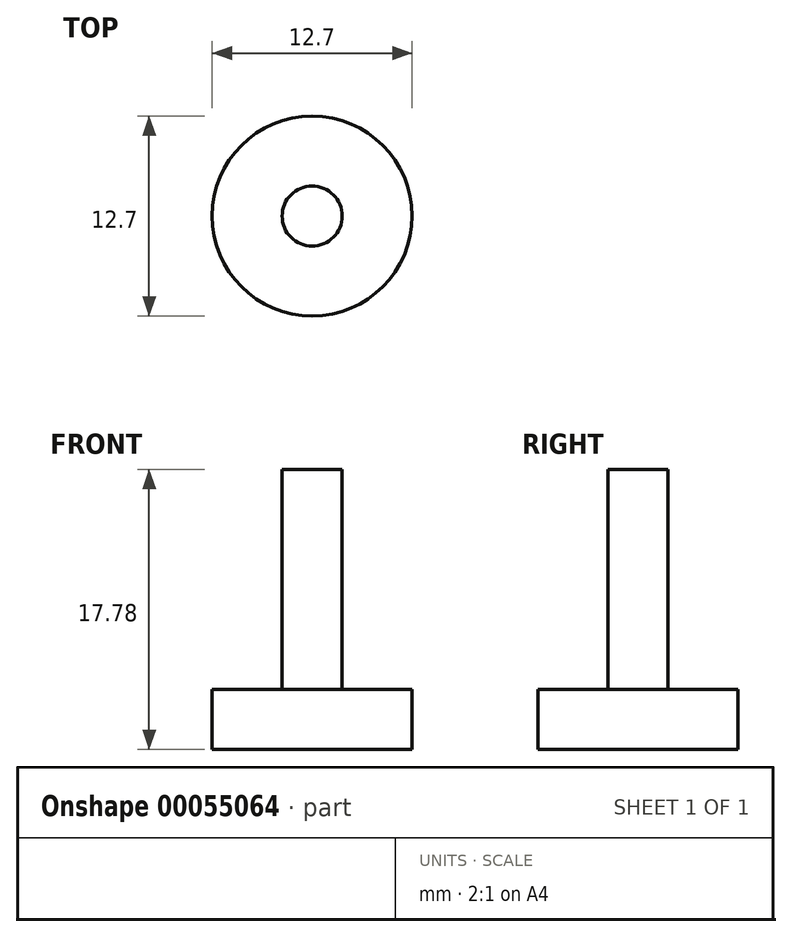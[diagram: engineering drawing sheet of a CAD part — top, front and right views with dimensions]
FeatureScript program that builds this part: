
annotation { "Feature Type Name" : "Feature", "Feature Type Description" : "" }
export const myFeature = defineFeature(function(context is Context, id is Id, definition is map)
    precondition{}
    {
        {
            var Q0;
            Q0=qCreatedBy(makeId("Top.planeOp"),FACE);
            var sketch = newSketch(context, id + "F0", { "sketchPlane" : qUnion([Q0])});
            skCircle(sketch, "E0", {"center": v(0, 0) * mm, "radius": 6.35 * mm});
            skSolve(sketch);
        }
        {
            var Q0;
            Q0=makeQuery(id+"F0.imprint","IMPRINT",FACE,{"disambiguationData":[TD([[makeQuery(id+"F0.imprint","IMPRINT",EDGE,{"derivedFrom":sQuery(id+"F0.wireOp",EDGE,"E0")}),1.0]])]});
            extrude(context, id + "F1", {"entities" : qUnion([Q0]), "oppositeDirection" : true, "depth" : 3.8 * mm});
        }
        {
            var Q0;
            Q0=makeQuery(id+"F1.opExtrude","CAP_FACE",FACE,{"disambiguationData":[OSD([sQuery(id+"F0.wireOp",EDGE,"E0")])],"isStart":true});
            var sketch = newSketch(context, id + "F2", { "sketchPlane" : qUnion([Q0])});
            skCircle(sketch, "E1", {"center": v(0, 0) * mm, "radius": 1.9 * mm});
            skSolve(sketch);
        }
        {
            var Q0;
            Q0 = qSketchRegion(id + "F2", true);
            extrude(context, id + "F3", {"entities" : qUnion([Q0]), "operationType" : NewBodyOperationType.ADD, "depth" : 13.97 * mm});
        }
    });
